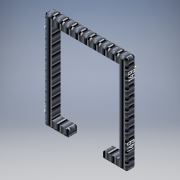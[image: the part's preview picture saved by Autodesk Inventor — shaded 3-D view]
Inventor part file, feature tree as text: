
AUTODESK INVENTOR PART (.ipt)
format: ipt  version: 2017 (Build 210142000, 142)  size: 228,352 bytes
history: native  units: in
note: dims shown in document units (in); Inventor stores cm internally (conversion verified against a paired STEP export)
features: sketch x3, extrude x1, fillet x1
ambient origin geometry x8: Origin, YZ Plane, XZ Plane, XY Plane, X Axis, Y Axis, Z Axis, Center Point
bodies: Solid1 (feature_tree)
feature tree (5):
  extrude  "Extrusion1"  Depth=33.1in
  fillet  "Fillet1"  Radius=6.6in
  sketch  "Sketch2"  dims[d3=6.6in]
  sketch  "Sketch3"  dims[d4=3.0in d5=3.5in d6=0.0in d7=0.75in]
  sketch  "Sketch1"  dims[d0=27.1in d1=33.1in d2=6.6in]
